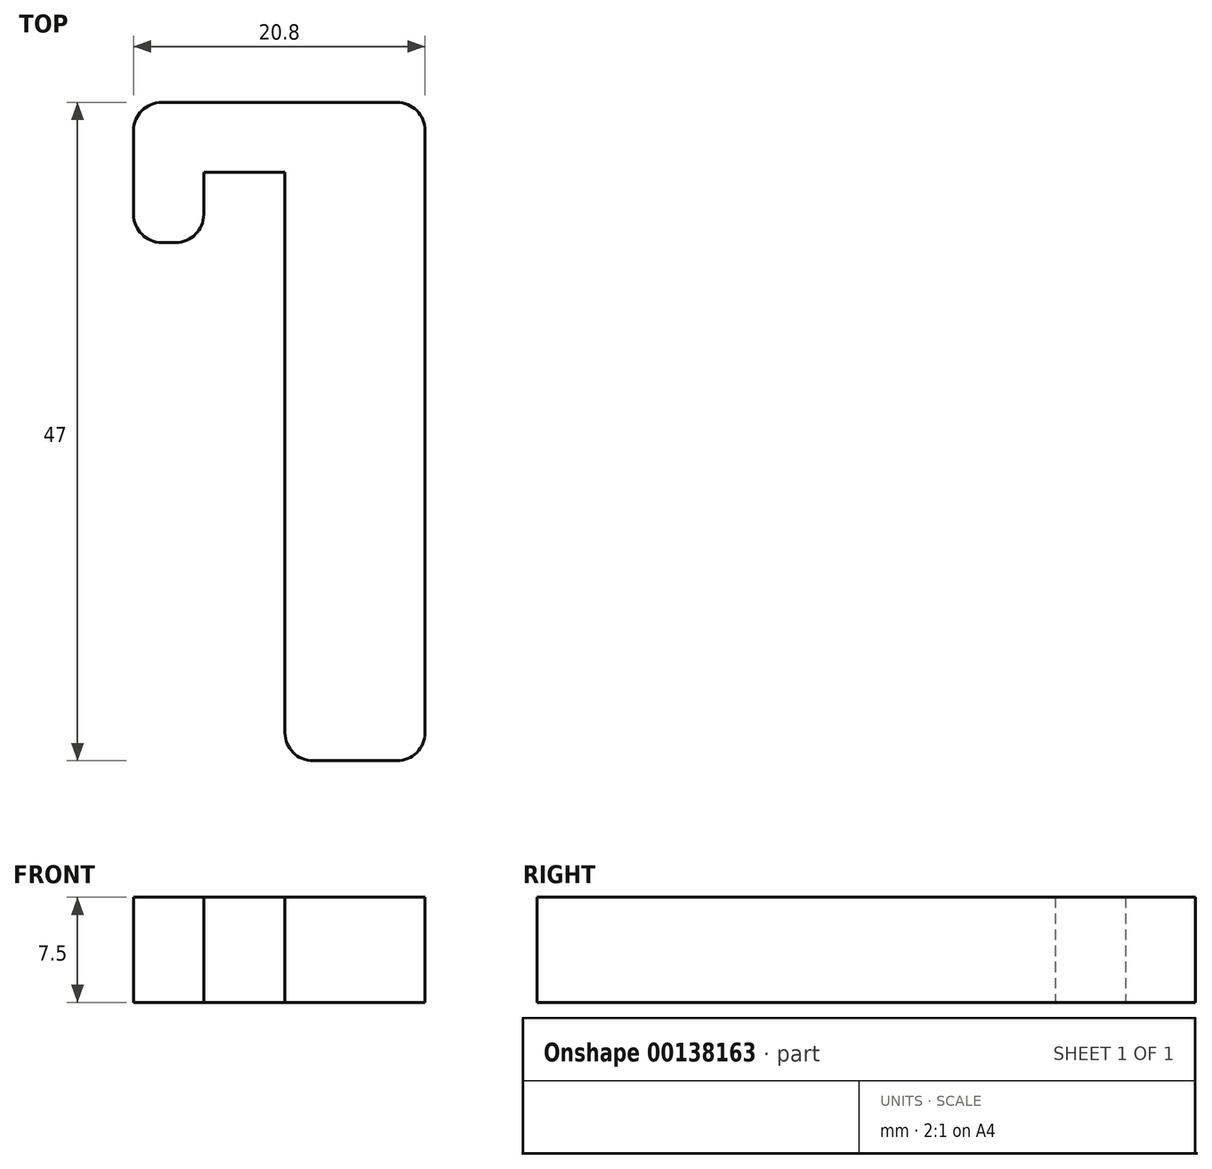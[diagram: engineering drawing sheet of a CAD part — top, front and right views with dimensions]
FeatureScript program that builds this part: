
annotation { "Feature Type Name" : "Feature", "Feature Type Description" : "" }
export const myFeature = defineFeature(function(context is Context, id is Id, definition is map)
    precondition{}
    {
        {
            var Q0;
            Q0=qCreatedBy(makeId("Top.planeOp"),FACE);
            var sketch = newSketch(context, id + "F0", { "sketchPlane" : qUnion([Q0])});
            skLineSegment(sketch, "E0", {"start": v(2, 0) * mm, "end": v(8, 0) * mm});
            skLineSegment(sketch, "E1", {"start": v(10, 2) * mm, "end": v(10, 45) * mm});
            skLineSegment(sketch, "E2", {"start": v(8, 47) * mm, "end": v(-8.8, 47) * mm});
            skLineSegment(sketch, "E3", {"start": v(-10.8, 45) * mm, "end": v(-10.8, 39) * mm});
            skLineSegment(sketch, "E4", {"start": v(-8.8, 37) * mm, "end": v(-7.8, 37) * mm});
            skLineSegment(sketch, "E5", {"start": v(-5.8, 39) * mm, "end": v(-5.8, 42) * mm});
            skLineSegment(sketch, "E6", {"start": v(-5.8, 42) * mm, "end": v(0, 42) * mm});
            skLineSegment(sketch, "E7", {"start": v(0, 42) * mm, "end": v(0, 2) * mm});
            skPoint(sketch, "E8.visualSharp", {"position": v(0, 0) * mm});
            skArc(sketch, "E8.filletArc", {"start": v(0, 2) * mm, "mid": v(0.59, 0.59) * mm, "end": v(2, 0) * mm});
            skPoint(sketch, "E9.visualSharp", {"position": v(10, 0) * mm});
            skArc(sketch, "E9.filletArc", {"start": v(8, 0) * mm, "mid": v(9.41, 0.59) * mm, "end": v(10, 2) * mm});
            skPoint(sketch, "E10.visualSharp", {"position": v(10, 47) * mm});
            skArc(sketch, "E10.filletArc", {"start": v(10, 45) * mm, "mid": v(9.41, 46.41) * mm, "end": v(8, 47) * mm});
            skPoint(sketch, "E11.visualSharp", {"position": v(-10.8, 47) * mm});
            skArc(sketch, "E11.filletArc", {"start": v(-8.8, 47) * mm, "mid": v(-10.21, 46.41) * mm, "end": v(-10.8, 45) * mm});
            skPoint(sketch, "E12.visualSharp", {"position": v(-10.8, 37) * mm});
            skArc(sketch, "E12.filletArc", {"start": v(-10.8, 39) * mm, "mid": v(-10.21, 37.59) * mm, "end": v(-8.8, 37) * mm});
            skPoint(sketch, "E13.visualSharp", {"position": v(-5.8, 37) * mm});
            skArc(sketch, "E13.filletArc", {"start": v(-7.8, 37) * mm, "mid": v(-6.39, 37.59) * mm, "end": v(-5.8, 39) * mm});
            skSolve(sketch);
        }
        {
            var Q0;
            Q0 = qSketchRegion(id + "F0", true);
            extrude(context, id + "F1", {"entities" : qUnion([Q0]), "depth" : 7.5 * mm});
        }
    });
